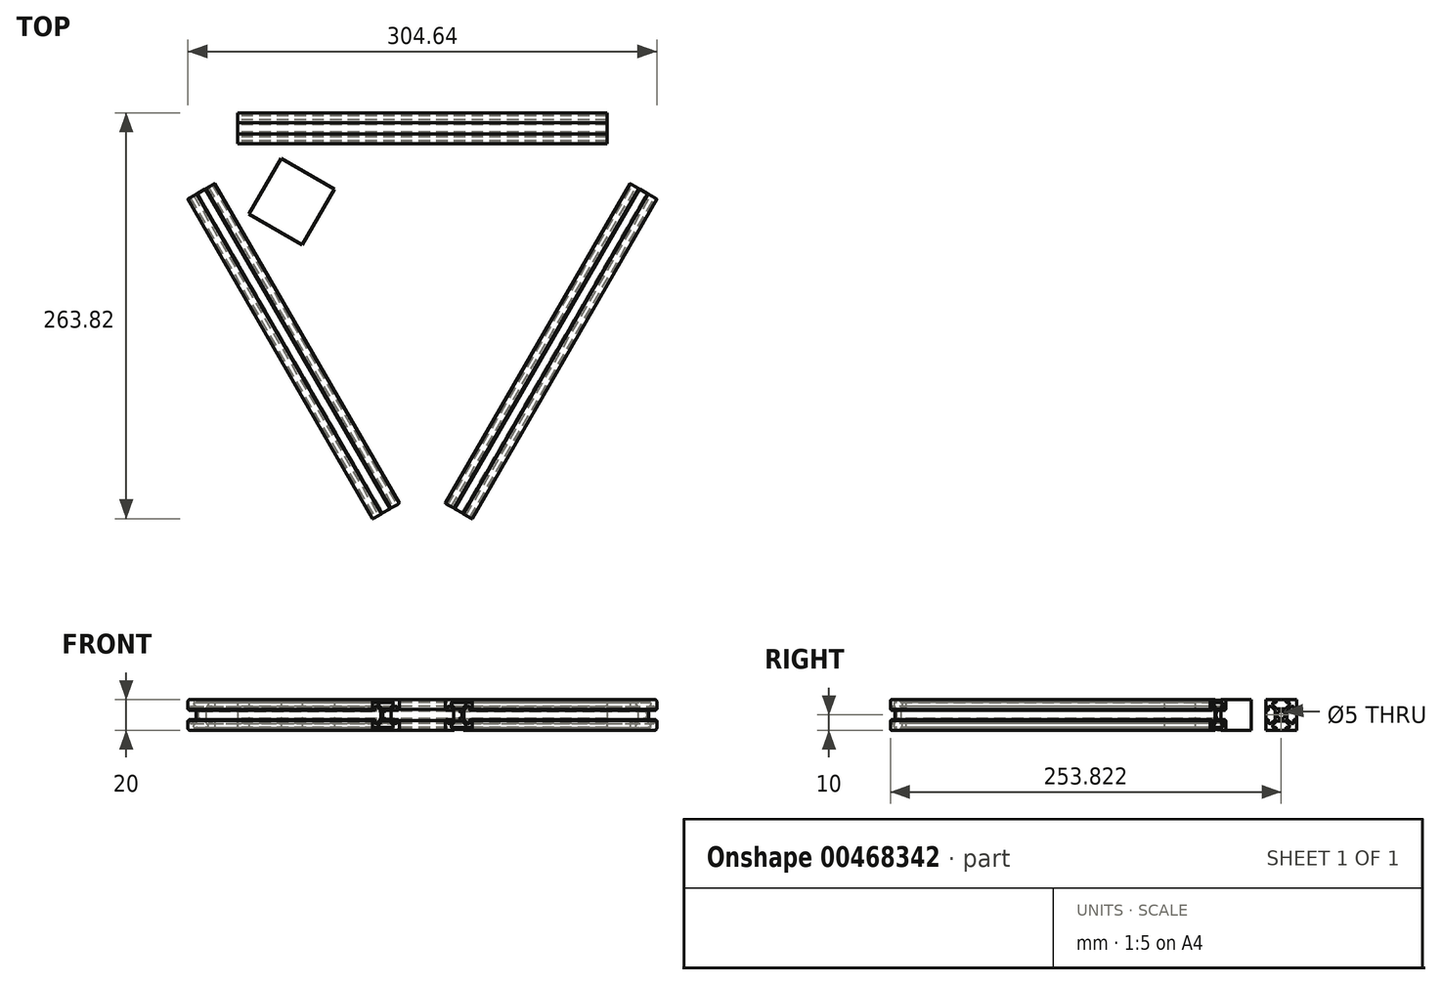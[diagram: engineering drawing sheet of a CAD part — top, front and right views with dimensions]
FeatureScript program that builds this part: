
annotation { "Feature Type Name" : "Feature", "Feature Type Description" : "" }
export const myFeature = defineFeature(function(context is Context, id is Id, definition is map)
    precondition{}
    {
        {
            var Q0;
            Q0=qCreatedBy(makeId("Top.planeOp"),FACE);
            var sketch = newSketch(context, id + "F0", { "sketchPlane" : qUnion([Q0])});
            skLineSegment(sketch, "E0.bottom", {"start": v(-120, 106.6) * mm, "end": v(120, 106.6) * mm});
            skLineSegment(sketch, "E0.top", {"start": v(-120, 86.6) * mm, "end": v(120, 86.6) * mm});
            skLineSegment(sketch, "E0.left", {"start": v(-120, 106.6) * mm, "end": v(-120, 86.6) * mm});
            skLineSegment(sketch, "E0.right", {"start": v(120, 106.6) * mm, "end": v(120, 86.6) * mm});
            skLineSegment(sketch, "E1", {"start": v(-117.74, 67.98) * mm, "end": v(117.74, 67.98) * mm, "construction": true});
            skLineSegment(sketch, "E2", {"start": v(117.74, 67.98) * mm, "end": v(0, -135.96) * mm, "construction": true});
            skLineSegment(sketch, "E3", {"start": v(0, -135.96) * mm, "end": v(-117.74, 67.98) * mm, "construction": true});
            skLineSegment(sketch, "E4", {"start": v(-117.74, 67.98) * mm, "end": v(58.87, -33.99) * mm, "construction": true});
            skLineSegment(sketch, "E5", {"start": v(58.87, -33.99) * mm, "end": v(0, -135.96) * mm, "construction": true});
            skLineSegment(sketch, "E6", {"start": v(0, 67.98) * mm, "end": v(0, -135.96) * mm, "construction": true});
            skLineSegment(sketch, "E7", {"start": v(117.74, 67.98) * mm, "end": v(-58.87, -33.99) * mm, "construction": true});
            skLineSegment(sketch, "E8.MirrorCS", {"start": v(-152.32, 50.62) * mm, "end": v(-32.32, -157.22) * mm});
            skLineSegment(sketch, "E9.MirrorCS", {"start": v(-135, 60.62) * mm, "end": v(-15, -147.22) * mm});
            skLineSegment(sketch, "E10.MirrorCS", {"start": v(-152.32, 50.62) * mm, "end": v(-135, 60.62) * mm});
            skLineSegment(sketch, "E11.MirrorCS", {"start": v(-32.32, -157.22) * mm, "end": v(-15, -147.22) * mm});
            skLineSegment(sketch, "E12.MirrorCS", {"start": v(32.32, -157.22) * mm, "end": v(152.32, 50.62) * mm});
            skLineSegment(sketch, "E13.MirrorCS", {"start": v(15, -147.22) * mm, "end": v(135, 60.62) * mm});
            skLineSegment(sketch, "E14.MirrorCS", {"start": v(32.32, -157.22) * mm, "end": v(15, -147.22) * mm});
            skLineSegment(sketch, "E15.MirrorCS", {"start": v(152.32, 50.62) * mm, "end": v(135, 60.62) * mm});
            skPoint(sketch, "E16", {"position": v(0, 0) * mm});
            skLineSegment(sketch, "E17", {"start": v(-187.79, 96.6) * mm, "end": v(190.4, 96.6) * mm, "construction": true});
            skPoint(sketch, "E17.startSnap0", {"position": v(-120, 96.6) * mm});
            skLineSegment(sketch, "E18.1.0", {"start": v(10.23, -210.93) * mm, "end": v(-178.86, 116.59) * mm, "construction": true});
            skLineSegment(sketch, "E18.2.0", {"start": v(177.55, 114.33) * mm, "end": v(-11.54, -213.19) * mm, "construction": true});
            skSolve(sketch);
        }
        {
            var Q0;
            Q0=makeQuery(id+"F0.imprint","IMPRINT",FACE,{"disambiguationData":[TD([[makeQuery(id+"F0.imprint","IMPRINT",EDGE,{"derivedFrom":sQuery(id+"F0.wireOp",EDGE,"E0.bottom")}),-1.0]])]});
            extrude(context, id + "F1", {"entities" : qUnion([Q0]), "offsetDistance" : 25 * mm, "depth" : 20 * mm});
        }
        {
            var Q0;
            Q0=makeQuery(id+"F1.opExtrude","SWEPT_FACE",FACE,{"disambiguationData":[OSD([sQuery(id+"F0.wireOp",EDGE,"E0.left")])]});
            var sketch = newSketch(context, id + "F2", { "sketchPlane" : qUnion([Q0])});
            skCircle(sketch, "E19", {"center": v(-96.6, 10) * mm, "radius": 2.5 * mm});
            skPoint(sketch, "E19.centerSnap0", {"position": v(-106.6, 10) * mm});
            skPoint(sketch, "E19.centerSnap1", {"position": v(-96.6, 20) * mm});
            skLineSegment(sketch, "E20.bottom", {"start": v(-86.6, 20) * mm, "end": v(-105.1, 20) * mm});
            skLineSegment(sketch, "E20.top", {"start": v(-86.6, 0) * mm, "end": v(-106.6, 0) * mm});
            skLineSegment(sketch, "E20.left", {"start": v(-86.6, 20) * mm, "end": v(-86.6, 0) * mm});
            skLineSegment(sketch, "E20.right", {"start": v(-106.6, 18.5) * mm, "end": v(-106.6, 0) * mm});
            skPoint(sketch, "E21.visualSharp", {"position": v(-106.6, 20) * mm});
            skArc(sketch, "E21.filletArc", {"start": v(-105.1, 20) * mm, "mid": v(-106.16, 19.56) * mm, "end": v(-106.6, 18.5) * mm});
            skLineSegment(sketch, "E22", {"start": v(-106.6, 20) * mm, "end": v(-100.5, 13.9) * mm, "construction": true});
            skLineSegment(sketch, "E23", {"start": v(-96.6, 20) * mm, "end": v(-96.6, 10) * mm, "construction": true});
            skLineSegment(sketch, "E24", {"start": v(-100.5, 13.9) * mm, "end": v(-96.6, 10) * mm, "construction": true});
            skLineSegment(sketch, "E25", {"start": v(-102.1, 17.9) * mm, "end": v(-102.1, 16.72) * mm});
            skLineSegment(sketch, "E26", {"start": v(-102.01, 16.51) * mm, "end": v(-99.5, 13.99) * mm});
            skLineSegment(sketch, "E27", {"start": v(-101.8, 18.2) * mm, "end": v(-100, 18.2) * mm});
            skLineSegment(sketch, "E28", {"start": v(-99.7, 18.5) * mm, "end": v(-99.7, 19.5) * mm});
            skLineSegment(sketch, "E29", {"start": v(-99.7, 19.5) * mm, "end": v(-100.2, 19.5) * mm});
            skLineSegment(sketch, "E30", {"start": v(-100.2, 19.5) * mm, "end": v(-100.2, 20) * mm});
            skLineSegment(sketch, "E31", {"start": v(-99.28, 13.9) * mm, "end": v(-96.6, 13.9) * mm});
            skPoint(sketch, "E32.visualSharp", {"position": v(-102.1, 18.2) * mm});
            skArc(sketch, "E32.filletArc", {"start": v(-101.8, 18.2) * mm, "mid": v(-102.01, 18.11) * mm, "end": v(-102.1, 17.9) * mm});
            skPoint(sketch, "E33.visualSharp", {"position": v(-102.1, 16.6) * mm});
            skArc(sketch, "E33.filletArc", {"start": v(-102.1, 16.72) * mm, "mid": v(-102.08, 16.6) * mm, "end": v(-102.01, 16.51) * mm});
            skPoint(sketch, "E34.visualSharp", {"position": v(-99.4, 13.9) * mm});
            skArc(sketch, "E34.filletArc", {"start": v(-99.5, 13.99) * mm, "mid": v(-99.4, 13.92) * mm, "end": v(-99.28, 13.9) * mm});
            skPoint(sketch, "E35.visualSharp", {"position": v(-99.7, 18.2) * mm});
            skArc(sketch, "E35.filletArc", {"start": v(-100, 18.2) * mm, "mid": v(-99.8, 18.29) * mm, "end": v(-99.7, 18.5) * mm});
            skLineSegment(sketch, "E36", {"start": v(-106.6, 10) * mm, "end": v(-96.6, 10) * mm, "construction": true});
            skLineSegment(sketch, "E37", {"start": v(-106.6, 0) * mm, "end": v(-96.6, 10) * mm, "construction": true});
            skArc(sketch, "E38.MirrorCS", {"start": v(-91.1, 16.72) * mm, "mid": v(-91.13, 16.6) * mm, "end": v(-91.2, 16.51) * mm});
            skArc(sketch, "E39.MirrorCS", {"start": v(-93.71, 13.99) * mm, "mid": v(-93.81, 13.92) * mm, "end": v(-93.93, 13.9) * mm});
            skLineSegment(sketch, "E40.MirrorCS", {"start": v(-93.5, 19.5) * mm, "end": v(-93, 19.5) * mm});
            skArc(sketch, "E41.MirrorCS", {"start": v(-93.2, 18.2) * mm, "mid": v(-93.41, 18.29) * mm, "end": v(-93.5, 18.5) * mm});
            skArc(sketch, "E42.MirrorCS", {"start": v(-91.4, 18.2) * mm, "mid": v(-91.2, 18.11) * mm, "end": v(-91.1, 17.9) * mm});
            skLineSegment(sketch, "E43.MirrorCS", {"start": v(-93, 19.5) * mm, "end": v(-93, 20) * mm});
            skPoint(sketch, "E44.MirrorP", {"position": v(-93.5, 18.2) * mm});
            skLineSegment(sketch, "E45.MirrorCS", {"start": v(-93.5, 18.5) * mm, "end": v(-93.5, 19.5) * mm});
            skLineSegment(sketch, "E46.MirrorCS", {"start": v(-86.6, 20) * mm, "end": v(-92.7, 13.9) * mm, "construction": true});
            skPoint(sketch, "E47.MirrorP", {"position": v(-93.8, 13.9) * mm});
            skPoint(sketch, "E48.MirrorP", {"position": v(-91.1, 16.6) * mm});
            skPoint(sketch, "E49.MirrorP", {"position": v(-86.6, 20) * mm});
            skArc(sketch, "E50.MirrorCS", {"start": v(-88.1, 20) * mm, "mid": v(-87.04, 19.56) * mm, "end": v(-86.6, 18.5) * mm});
            skLineSegment(sketch, "E51.MirrorCS", {"start": v(-91.1, 17.9) * mm, "end": v(-91.1, 16.72) * mm});
            skLineSegment(sketch, "E52.MirrorCS", {"start": v(-91.2, 16.51) * mm, "end": v(-93.71, 13.99) * mm});
            skPoint(sketch, "E53.MirrorP", {"position": v(-91.1, 18.2) * mm});
            skLineSegment(sketch, "E54.MirrorCS", {"start": v(-91.4, 18.2) * mm, "end": v(-93.2, 18.2) * mm});
            skLineSegment(sketch, "E55.MirrorCS", {"start": v(-93.93, 13.9) * mm, "end": v(-96.6, 13.9) * mm});
            skArc(sketch, "E56.MirrorCS", {"start": v(-89.88, 15.5) * mm, "mid": v(-90, 15.48) * mm, "end": v(-90.1, 15.41) * mm});
            skArc(sketch, "E57.MirrorCS", {"start": v(-92.61, 12.89) * mm, "mid": v(-92.68, 12.8) * mm, "end": v(-92.7, 12.68) * mm});
            skLineSegment(sketch, "E58.MirrorCS", {"start": v(-87.1, 13.6) * mm, "end": v(-86.6, 13.6) * mm});
            skArc(sketch, "E59.MirrorCS", {"start": v(-88.4, 15.2) * mm, "mid": v(-88.5, 15.41) * mm, "end": v(-88.7, 15.5) * mm});
            skLineSegment(sketch, "E60.MirrorCS", {"start": v(-87.1, 13.1) * mm, "end": v(-87.1, 13.6) * mm});
            skArc(sketch, "E61.MirrorCS", {"start": v(-88.4, 13.4) * mm, "mid": v(-88.31, 13.19) * mm, "end": v(-88.1, 13.1) * mm});
            skPoint(sketch, "E62.MirrorP", {"position": v(-88.4, 13.1) * mm});
            skArc(sketch, "E63.MirrorCS", {"start": v(-86.6, 18.5) * mm, "mid": v(-87.04, 19.56) * mm, "end": v(-88.1, 20) * mm});
            skLineSegment(sketch, "E64.MirrorCS", {"start": v(-88.4, 15.2) * mm, "end": v(-88.4, 13.4) * mm});
            skPoint(sketch, "E65.MirrorP", {"position": v(-92.7, 12.8) * mm});
            skLineSegment(sketch, "E66.MirrorCS", {"start": v(-88.1, 13.1) * mm, "end": v(-87.1, 13.1) * mm});
            skLineSegment(sketch, "E67.MirrorCS", {"start": v(-90.1, 15.41) * mm, "end": v(-92.61, 12.89) * mm});
            skLineSegment(sketch, "E68.MirrorCS", {"start": v(-88.7, 15.5) * mm, "end": v(-89.88, 15.5) * mm});
            skPoint(sketch, "E69.MirrorP", {"position": v(-90, 15.5) * mm});
            skPoint(sketch, "E70.MirrorP", {"position": v(-88.4, 15.5) * mm});
            skPoint(sketch, "E71.MirrorP", {"position": v(-86.6, 10) * mm});
            skLineSegment(sketch, "E72.MirrorCS", {"start": v(-92.7, 12.68) * mm, "end": v(-92.7, 10) * mm});
            skArc(sketch, "E73.MirrorCS", {"start": v(-104.8, 15.2) * mm, "mid": v(-104.71, 15.41) * mm, "end": v(-104.5, 15.5) * mm});
            skArc(sketch, "E74.MirrorCS", {"start": v(-103.33, 15.5) * mm, "mid": v(-103.21, 15.48) * mm, "end": v(-103.11, 15.41) * mm});
            skArc(sketch, "E75.MirrorCS", {"start": v(-100.6, 12.89) * mm, "mid": v(-100.53, 12.8) * mm, "end": v(-100.5, 12.68) * mm});
            skLineSegment(sketch, "E76.MirrorCS", {"start": v(-105.1, 13.1) * mm, "end": v(-106.1, 13.1) * mm});
            skLineSegment(sketch, "E77.MirrorCS", {"start": v(-106.1, 13.6) * mm, "end": v(-106.6, 13.6) * mm});
            skArc(sketch, "E78.MirrorCS", {"start": v(-104.8, 13.4) * mm, "mid": v(-104.9, 13.19) * mm, "end": v(-105.1, 13.1) * mm});
            skLineSegment(sketch, "E79.MirrorCS", {"start": v(-106.1, 13.1) * mm, "end": v(-106.1, 13.6) * mm});
            skLineSegment(sketch, "E80.MirrorCS", {"start": v(-104.8, 15.2) * mm, "end": v(-104.8, 13.4) * mm});
            skPoint(sketch, "E81.MirrorP", {"position": v(-100.5, 12.8) * mm});
            skPoint(sketch, "E82.MirrorP", {"position": v(-103.2, 15.5) * mm});
            skLineSegment(sketch, "E83.MirrorCS", {"start": v(-103.11, 15.41) * mm, "end": v(-100.6, 12.89) * mm});
            skLineSegment(sketch, "E84.MirrorCS", {"start": v(-100.5, 12.68) * mm, "end": v(-100.5, 10) * mm});
            skLineSegment(sketch, "E85.MirrorCS", {"start": v(-104.5, 15.5) * mm, "end": v(-103.33, 15.5) * mm});
            skPoint(sketch, "E86.MirrorP", {"position": v(-104.8, 15.5) * mm});
            skArc(sketch, "E87.MirrorCS", {"start": v(-106.6, 18.5) * mm, "mid": v(-106.16, 19.56) * mm, "end": v(-105.1, 20) * mm});
            skPoint(sketch, "E88.MirrorP", {"position": v(-104.8, 13.1) * mm});
            skArc(sketch, "E89.MirrorCS", {"start": v(-89.88, 4.5) * mm, "mid": v(-90, 4.52) * mm, "end": v(-90.1, 4.59) * mm});
            skArc(sketch, "E90.MirrorCS", {"start": v(-100.6, 7.11) * mm, "mid": v(-100.53, 7.2) * mm, "end": v(-100.5, 7.32) * mm});
            skArc(sketch, "E91.MirrorCS", {"start": v(-103.33, 4.5) * mm, "mid": v(-103.21, 4.52) * mm, "end": v(-103.11, 4.59) * mm});
            skArc(sketch, "E92.MirrorCS", {"start": v(-93.71, 6.01) * mm, "mid": v(-93.81, 6.08) * mm, "end": v(-93.93, 6.1) * mm});
            skArc(sketch, "E93.MirrorCS", {"start": v(-99.5, 6.01) * mm, "mid": v(-99.4, 6.08) * mm, "end": v(-99.28, 6.1) * mm});
            skArc(sketch, "E94.MirrorCS", {"start": v(-91.1, 3.28) * mm, "mid": v(-91.13, 3.4) * mm, "end": v(-91.2, 3.49) * mm});
            skArc(sketch, "E95.MirrorCS", {"start": v(-92.61, 7.11) * mm, "mid": v(-92.68, 7.2) * mm, "end": v(-92.7, 7.32) * mm});
            skArc(sketch, "E96.MirrorCS", {"start": v(-102.1, 3.28) * mm, "mid": v(-102.08, 3.4) * mm, "end": v(-102.01, 3.49) * mm});
            skArc(sketch, "E97.MirrorCS", {"start": v(-104.8, 6.6) * mm, "mid": v(-104.9, 6.81) * mm, "end": v(-105.1, 6.9) * mm});
            skLineSegment(sketch, "E98.MirrorCS", {"start": v(-105.1, 6.9) * mm, "end": v(-106.1, 6.9) * mm});
            skLineSegment(sketch, "E99.MirrorCS", {"start": v(-99.7, 1.5) * mm, "end": v(-99.7, 0.5) * mm});
            skLineSegment(sketch, "E100.MirrorCS", {"start": v(-99.7, 0.5) * mm, "end": v(-100.2, 0.5) * mm});
            skLineSegment(sketch, "E101.MirrorCS", {"start": v(-93.5, 0.5) * mm, "end": v(-93, 0.5) * mm});
            skArc(sketch, "E102.MirrorCS", {"start": v(-101.8, 1.8) * mm, "mid": v(-102.01, 1.89) * mm, "end": v(-102.1, 2.1) * mm});
            skLineSegment(sketch, "E103.MirrorCS", {"start": v(-106.1, 6.9) * mm, "end": v(-106.1, 6.4) * mm});
            skLineSegment(sketch, "E104.MirrorCS", {"start": v(-87.1, 6.9) * mm, "end": v(-87.1, 6.4) * mm});
            skLineSegment(sketch, "E105.MirrorCS", {"start": v(-93.5, 1.5) * mm, "end": v(-93.5, 0.5) * mm});
            skArc(sketch, "E106.MirrorCS", {"start": v(-88.4, 6.6) * mm, "mid": v(-88.31, 6.81) * mm, "end": v(-88.1, 6.9) * mm});
            skArc(sketch, "E107.MirrorCS", {"start": v(-104.8, 4.8) * mm, "mid": v(-104.71, 4.59) * mm, "end": v(-104.5, 4.5) * mm});
            skArc(sketch, "E108.MirrorCS", {"start": v(-91.4, 1.8) * mm, "mid": v(-91.2, 1.89) * mm, "end": v(-91.1, 2.1) * mm});
            skArc(sketch, "E109.MirrorCS", {"start": v(-93.2, 1.8) * mm, "mid": v(-93.41, 1.71) * mm, "end": v(-93.5, 1.5) * mm});
            skArc(sketch, "E110.MirrorCS", {"start": v(-100, 1.8) * mm, "mid": v(-99.8, 1.71) * mm, "end": v(-99.7, 1.5) * mm});
            skArc(sketch, "E111.MirrorCS", {"start": v(-88.4, 4.8) * mm, "mid": v(-88.5, 4.59) * mm, "end": v(-88.7, 4.5) * mm});
            skLineSegment(sketch, "E112.MirrorCS", {"start": v(-93, 0.5) * mm, "end": v(-93, 0) * mm});
            skPoint(sketch, "E113.MirrorP", {"position": v(-86.6, 0) * mm});
            skLineSegment(sketch, "E114.MirrorCS", {"start": v(-87.1, 6.4) * mm, "end": v(-86.6, 6.4) * mm});
            skArc(sketch, "E115.MirrorCS", {"start": v(-88.1, 0) * mm, "mid": v(-87.04, 0.44) * mm, "end": v(-86.6, 1.5) * mm});
            skLineSegment(sketch, "E116.MirrorCS", {"start": v(-100.2, 0.5) * mm, "end": v(-100.2, 0) * mm});
            skArc(sketch, "E117.MirrorCS", {"start": v(-105.1, 0) * mm, "mid": v(-106.16, 0.44) * mm, "end": v(-106.6, 1.5) * mm});
            skLineSegment(sketch, "E118.MirrorCS", {"start": v(-106.1, 6.4) * mm, "end": v(-106.6, 6.4) * mm});
            skPoint(sketch, "E119.MirrorP", {"position": v(-106.6, 0) * mm});
            skPoint(sketch, "E120.MirrorP", {"position": v(-103.2, 4.5) * mm});
            skPoint(sketch, "E121.MirrorP", {"position": v(-90, 4.5) * mm});
            skPoint(sketch, "E122.MirrorP", {"position": v(-102.1, 3.4) * mm});
            skLineSegment(sketch, "E123.MirrorCS", {"start": v(-88.1, 6.9) * mm, "end": v(-87.1, 6.9) * mm});
            skArc(sketch, "E124.MirrorCS", {"start": v(-106.6, 1.5) * mm, "mid": v(-106.16, 0.44) * mm, "end": v(-105.1, 0) * mm});
            skPoint(sketch, "E125.MirrorP", {"position": v(-92.7, 7.2) * mm});
            skPoint(sketch, "E126.MirrorP", {"position": v(-91.1, 3.4) * mm});
            skArc(sketch, "E127.MirrorCS", {"start": v(-86.6, 1.5) * mm, "mid": v(-87.04, 0.44) * mm, "end": v(-88.1, 0) * mm});
            skLineSegment(sketch, "E128.MirrorCS", {"start": v(-100.5, 6.1) * mm, "end": v(-96.6, 10) * mm, "construction": true});
            skLineSegment(sketch, "E129.MirrorCS", {"start": v(-96.6, 0) * mm, "end": v(-96.6, 10) * mm, "construction": true});
            skLineSegment(sketch, "E130.MirrorCS", {"start": v(-86.6, 0) * mm, "end": v(-105.1, 0) * mm});
            skLineSegment(sketch, "E131.MirrorCS", {"start": v(-99.28, 6.1) * mm, "end": v(-96.6, 6.1) * mm});
            skLineSegment(sketch, "E132.MirrorCS", {"start": v(-91.4, 1.8) * mm, "end": v(-93.2, 1.8) * mm});
            skPoint(sketch, "E133.MirrorP", {"position": v(-104.8, 6.9) * mm});
            skPoint(sketch, "E134.MirrorP", {"position": v(-99.7, 1.8) * mm});
            skLineSegment(sketch, "E135.MirrorCS", {"start": v(-92.7, 7.32) * mm, "end": v(-92.7, 10) * mm});
            skPoint(sketch, "E136.MirrorP", {"position": v(-100.5, 7.2) * mm});
            skPoint(sketch, "E137.MirrorP", {"position": v(-91.1, 1.8) * mm});
            skPoint(sketch, "E138.MirrorP", {"position": v(-93.5, 1.8) * mm});
            skLineSegment(sketch, "E139.MirrorCS", {"start": v(-103.11, 4.59) * mm, "end": v(-100.6, 7.11) * mm});
            skPoint(sketch, "E140.MirrorP", {"position": v(-88.4, 4.5) * mm});
            skPoint(sketch, "E141.MirrorP", {"position": v(-99.4, 6.1) * mm});
            skPoint(sketch, "E142.MirrorP", {"position": v(-96.6, 0) * mm});
            skPoint(sketch, "E143.MirrorP", {"position": v(-104.8, 4.5) * mm});
            skLineSegment(sketch, "E144.MirrorCS", {"start": v(-90.1, 4.59) * mm, "end": v(-92.61, 7.11) * mm});
            skLineSegment(sketch, "E145.MirrorCS", {"start": v(-91.1, 2.1) * mm, "end": v(-91.1, 3.28) * mm});
            skLineSegment(sketch, "E146.MirrorCS", {"start": v(-86.6, 0) * mm, "end": v(-92.7, 6.1) * mm, "construction": true});
            skLineSegment(sketch, "E147.MirrorCS", {"start": v(-93.93, 6.1) * mm, "end": v(-96.6, 6.1) * mm});
            skLineSegment(sketch, "E148.MirrorCS", {"start": v(-100.5, 7.32) * mm, "end": v(-100.5, 10) * mm});
            skPoint(sketch, "E149.MirrorP", {"position": v(-88.4, 6.9) * mm});
            skLineSegment(sketch, "E150.MirrorCS", {"start": v(-88.7, 4.5) * mm, "end": v(-89.88, 4.5) * mm});
            skPoint(sketch, "E151.MirrorP", {"position": v(-93.8, 6.1) * mm});
            skLineSegment(sketch, "E152.MirrorCS", {"start": v(-88.4, 4.8) * mm, "end": v(-88.4, 6.6) * mm});
            skLineSegment(sketch, "E153.MirrorCS", {"start": v(-104.8, 4.8) * mm, "end": v(-104.8, 6.6) * mm});
            skLineSegment(sketch, "E154.MirrorCS", {"start": v(-102.01, 3.49) * mm, "end": v(-99.5, 6.01) * mm});
            skLineSegment(sketch, "E155.MirrorCS", {"start": v(-101.8, 1.8) * mm, "end": v(-100, 1.8) * mm});
            skLineSegment(sketch, "E156.MirrorCS", {"start": v(-104.5, 4.5) * mm, "end": v(-103.33, 4.5) * mm});
            skPoint(sketch, "E157.MirrorP", {"position": v(-102.1, 1.8) * mm});
            skLineSegment(sketch, "E158.MirrorCS", {"start": v(-106.6, 0) * mm, "end": v(-100.5, 6.1) * mm, "construction": true});
            skLineSegment(sketch, "E159.MirrorCS", {"start": v(-102.1, 2.1) * mm, "end": v(-102.1, 3.28) * mm});
            skLineSegment(sketch, "E160.MirrorCS", {"start": v(-91.2, 3.49) * mm, "end": v(-93.71, 6.01) * mm});
            skSolve(sketch);
        }
        {
            var Q0;
            Q0=makeQuery(id+"F2.imprint","IMPRINT",FACE,{"disambiguationData":[TD([[makeQuery(id+"F2.imprint","IMPRINT",EDGE,{"derivedFrom":sQuery(id+"F2.wireOp",EDGE,"E19")}),-1.0]])]});
            extrude(context, id + "F3", {"entities" : qUnion([Q0]), "oppositeDirection" : true, "depth" : 240 * mm});
        }
        {
            var Q0;
            Q0=qCreatedBy(makeId("Right.planeOp"),FACE);
            var sketch = newSketch(context, id + "F4", { "sketchPlane" : qUnion([Q0])});
            skLineSegment(sketch, "E161", {"start": v(0, 0) * mm, "end": v(0, 47.33) * mm});
            skSolve(sketch);
        }
        {
            var Q0;
            Q0=makeQuery(id+"F3.opExtrude","SWEPT_BODY",BODY,{"disambiguationData":[OSD([sQuery(id+"F2.wireOp",EDGE,"E19"),sQuery(id+"F2.wireOp",EDGE,"E20.bottom"),sQuery(id+"F2.wireOp",EDGE,"E20.left"),sQuery(id+"F2.wireOp",EDGE,"E20.right"),sQuery(id+"F2.wireOp",EDGE,"E25"),sQuery(id+"F2.wireOp",EDGE,"E26"),sQuery(id+"F2.wireOp",EDGE,"E27"),sQuery(id+"F2.wireOp",EDGE,"E28"),sQuery(id+"F2.wireOp",EDGE,"E29"),sQuery(id+"F2.wireOp",EDGE,"E30"),sQuery(id+"F2.wireOp",EDGE,"E31"),sQuery(id+"F2.wireOp",EDGE,"E32.filletArc"),sQuery(id+"F2.wireOp",EDGE,"E33.filletArc"),sQuery(id+"F2.wireOp",EDGE,"E34.filletArc"),sQuery(id+"F2.wireOp",EDGE,"E35.filletArc"),sQuery(id+"F2.wireOp",EDGE,"E38.MirrorCS"),sQuery(id+"F2.wireOp",EDGE,"E39.MirrorCS"),sQuery(id+"F2.wireOp",EDGE,"E40.MirrorCS"),sQuery(id+"F2.wireOp",EDGE,"E41.MirrorCS"),sQuery(id+"F2.wireOp",EDGE,"E42.MirrorCS"),sQuery(id+"F2.wireOp",EDGE,"E43.MirrorCS"),sQuery(id+"F2.wireOp",EDGE,"E45.MirrorCS"),sQuery(id+"F2.wireOp",EDGE,"E51.MirrorCS"),sQuery(id+"F2.wireOp",EDGE,"E52.MirrorCS"),sQuery(id+"F2.wireOp",EDGE,"E54.MirrorCS"),sQuery(id+"F2.wireOp",EDGE,"E55.MirrorCS"),sQuery(id+"F2.wireOp",EDGE,"E56.MirrorCS"),sQuery(id+"F2.wireOp",EDGE,"E57.MirrorCS"),sQuery(id+"F2.wireOp",EDGE,"E58.MirrorCS"),sQuery(id+"F2.wireOp",EDGE,"E59.MirrorCS"),sQuery(id+"F2.wireOp",EDGE,"E60.MirrorCS"),sQuery(id+"F2.wireOp",EDGE,"E61.MirrorCS"),sQuery(id+"F2.wireOp",EDGE,"E63.MirrorCS"),sQuery(id+"F2.wireOp",EDGE,"E64.MirrorCS"),sQuery(id+"F2.wireOp",EDGE,"E66.MirrorCS"),sQuery(id+"F2.wireOp",EDGE,"E67.MirrorCS"),sQuery(id+"F2.wireOp",EDGE,"E68.MirrorCS"),sQuery(id+"F2.wireOp",EDGE,"E72.MirrorCS"),sQuery(id+"F2.wireOp",EDGE,"E73.MirrorCS"),sQuery(id+"F2.wireOp",EDGE,"E74.MirrorCS"),sQuery(id+"F2.wireOp",EDGE,"E75.MirrorCS"),sQuery(id+"F2.wireOp",EDGE,"E76.MirrorCS"),sQuery(id+"F2.wireOp",EDGE,"E77.MirrorCS"),sQuery(id+"F2.wireOp",EDGE,"E78.MirrorCS"),sQuery(id+"F2.wireOp",EDGE,"E79.MirrorCS"),sQuery(id+"F2.wireOp",EDGE,"E80.MirrorCS"),sQuery(id+"F2.wireOp",EDGE,"E83.MirrorCS"),sQuery(id+"F2.wireOp",EDGE,"E84.MirrorCS"),sQuery(id+"F2.wireOp",EDGE,"E85.MirrorCS"),sQuery(id+"F2.wireOp",EDGE,"E87.MirrorCS"),sQuery(id+"F2.wireOp",EDGE,"E89.MirrorCS"),sQuery(id+"F2.wireOp",EDGE,"E90.MirrorCS"),sQuery(id+"F2.wireOp",EDGE,"E91.MirrorCS"),sQuery(id+"F2.wireOp",EDGE,"E92.MirrorCS"),sQuery(id+"F2.wireOp",EDGE,"E93.MirrorCS"),sQuery(id+"F2.wireOp",EDGE,"E94.MirrorCS"),sQuery(id+"F2.wireOp",EDGE,"E95.MirrorCS"),sQuery(id+"F2.wireOp",EDGE,"E96.MirrorCS"),sQuery(id+"F2.wireOp",EDGE,"E97.MirrorCS"),sQuery(id+"F2.wireOp",EDGE,"E98.MirrorCS"),sQuery(id+"F2.wireOp",EDGE,"E99.MirrorCS"),sQuery(id+"F2.wireOp",EDGE,"E100.MirrorCS"),sQuery(id+"F2.wireOp",EDGE,"E101.MirrorCS"),sQuery(id+"F2.wireOp",EDGE,"E102.MirrorCS"),sQuery(id+"F2.wireOp",EDGE,"E103.MirrorCS"),sQuery(id+"F2.wireOp",EDGE,"E104.MirrorCS"),sQuery(id+"F2.wireOp",EDGE,"E105.MirrorCS"),sQuery(id+"F2.wireOp",EDGE,"E106.MirrorCS"),sQuery(id+"F2.wireOp",EDGE,"E107.MirrorCS"),sQuery(id+"F2.wireOp",EDGE,"E108.MirrorCS"),sQuery(id+"F2.wireOp",EDGE,"E109.MirrorCS"),sQuery(id+"F2.wireOp",EDGE,"E110.MirrorCS"),sQuery(id+"F2.wireOp",EDGE,"E111.MirrorCS"),sQuery(id+"F2.wireOp",EDGE,"E112.MirrorCS"),sQuery(id+"F2.wireOp",EDGE,"E114.MirrorCS"),sQuery(id+"F2.wireOp",EDGE,"E116.MirrorCS"),sQuery(id+"F2.wireOp",EDGE,"E118.MirrorCS"),sQuery(id+"F2.wireOp",EDGE,"E123.MirrorCS"),sQuery(id+"F2.wireOp",EDGE,"E124.MirrorCS"),sQuery(id+"F2.wireOp",EDGE,"E127.MirrorCS"),sQuery(id+"F2.wireOp",EDGE,"E130.MirrorCS"),sQuery(id+"F2.wireOp",EDGE,"E131.MirrorCS"),sQuery(id+"F2.wireOp",EDGE,"E132.MirrorCS"),sQuery(id+"F2.wireOp",EDGE,"E135.MirrorCS"),sQuery(id+"F2.wireOp",EDGE,"E139.MirrorCS"),sQuery(id+"F2.wireOp",EDGE,"E144.MirrorCS"),sQuery(id+"F2.wireOp",EDGE,"E145.MirrorCS"),sQuery(id+"F2.wireOp",EDGE,"E147.MirrorCS"),sQuery(id+"F2.wireOp",EDGE,"E148.MirrorCS"),sQuery(id+"F2.wireOp",EDGE,"E150.MirrorCS"),sQuery(id+"F2.wireOp",EDGE,"E152.MirrorCS"),sQuery(id+"F2.wireOp",EDGE,"E153.MirrorCS"),sQuery(id+"F2.wireOp",EDGE,"E154.MirrorCS"),sQuery(id+"F2.wireOp",EDGE,"E155.MirrorCS"),sQuery(id+"F2.wireOp",EDGE,"E156.MirrorCS"),sQuery(id+"F2.wireOp",EDGE,"E159.MirrorCS"),sQuery(id+"F2.wireOp",EDGE,"E160.MirrorCS")])]});
            var Q1;
            Q1=sQuery(id+"F4.wireOp",EDGE,"E161");
            circularPattern(context, id + "F5", {"entities" : qUnion([Q0]), "axis" : qUnion([Q1]), "angle" : 360 * degree, "instanceCount" : 3, "equalSpace" : true});
        }
        {
            var Q0;
            Q0=qCreatedBy(makeId("Top.planeOp"),FACE);
            var sketch = newSketch(context, id + "F6", { "sketchPlane" : qUnion([Q0])});
            skCircle(sketch, "E162.cCircle", {"center": v(0, 0) * mm, "radius": 77.94 * mm, "construction": true});
            skLineSegment(sketch, "E162.0", {"start": v(45, 77.94) * mm, "end": v(90, 0) * mm, "construction": true});
            skLineSegment(sketch, "E162.1", {"start": v(90, 0) * mm, "end": v(45, -77.94) * mm, "construction": true});
            skLineSegment(sketch, "E162.2", {"start": v(45, -77.94) * mm, "end": v(-45, -77.94) * mm, "construction": true});
            skLineSegment(sketch, "E162.3", {"start": v(-45, -77.94) * mm, "end": v(-90, 0) * mm, "construction": true});
            skLineSegment(sketch, "E162.4", {"start": v(-90, 0) * mm, "end": v(-45, 77.94) * mm, "construction": true});
            skLineSegment(sketch, "E162.5", {"start": v(-45, 77.94) * mm, "end": v(45, 77.94) * mm, "construction": true});
            skPoint(sketch, "E162.0.midPoint", {"position": v(67.5, 38.97) * mm});
            skLineSegment(sketch, "E163.bottom", {"start": v(-50, 50) * mm, "end": v(50, 50) * mm});
            skLineSegment(sketch, "E163.top", {"start": v(-50, -50) * mm, "end": v(50, -50) * mm});
            skLineSegment(sketch, "E163.left", {"start": v(-50, 50) * mm, "end": v(-50, -50) * mm});
            skLineSegment(sketch, "E163.right", {"start": v(50, 50) * mm, "end": v(50, -50) * mm});
            skLineSegment(sketch, "E164", {"start": v(-50, 50) * mm, "end": v(50, -50) * mm, "construction": true});
            skLineSegment(sketch, "E165", {"start": v(-78, 20.78) * mm, "end": v(-112.64, 40.78) * mm});
            skLineSegment(sketch, "E166", {"start": v(-112.64, 40.78) * mm, "end": v(-91.64, 77.16) * mm});
            skLineSegment(sketch, "E167", {"start": v(-91.64, 77.16) * mm, "end": v(-57, 57.16) * mm});
            skPoint(sketch, "E168", {"position": v(-102.14, 58.97) * mm});
            skLineSegment(sketch, "E169", {"start": v(-78, 20.78) * mm, "end": v(-57, 57.16) * mm});
            skSolve(sketch);
        }
        {
            var Q0;
            Q0=makeQuery(id+"F6.imprint","IMPRINT",FACE,{"disambiguationData":[TD([[makeQuery(id+"F6.imprint","IMPRINT",EDGE,{"derivedFrom":sQuery(id+"F6.wireOp",EDGE,"E165")}),-1.0]])]});
            var Q1;
            {var subQ0=sQuery(id+"F2.wireOp",EDGE,"E20.bottom");Q1=makeQuery(id+"F3.opExtrude","SWEPT_FACE",FACE,{"disambiguationData":[OSD([subQ0]),TDD([makeQuery(id+"F2.imprint","IMPRINT",EDGE,{"disambiguationData":[TD([[makeQuery(id+"F2.imprint","INTERSECT",VERTEX,{"derivedFrom":[subQ0,sQuery(id+"F2.wireOp",EDGE,"E43.MirrorCS")]}),-1.0]])],"derivedFrom":subQ0})])]});}
            extrude(context, id + "F7", {"entities" : qUnion([Q0]), "endBound" : BoundingType.UP_TO_SURFACE, "depth" : 25 * mm, "endBoundEntityFace" : qUnion([Q1]), "offsetDistance" : 25 * mm});
        }
    });
